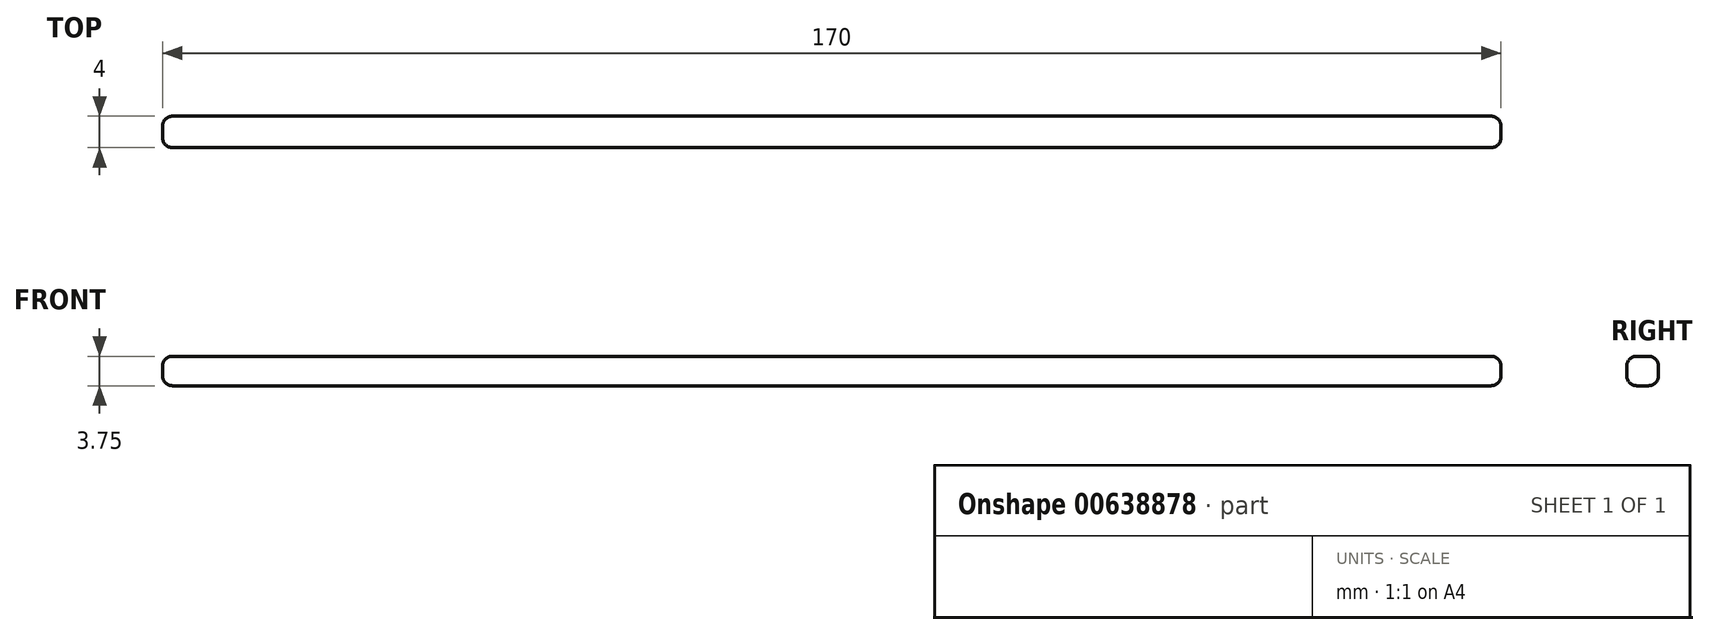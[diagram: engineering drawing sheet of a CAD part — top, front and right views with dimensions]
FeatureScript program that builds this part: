
annotation { "Feature Type Name" : "Feature", "Feature Type Description" : "" }
export const myFeature = defineFeature(function(context is Context, id is Id, definition is map)
    precondition{}
    {
        {
            var Q0;
            Q0=qCreatedBy(makeId("Top.planeOp"),FACE);
            var sketch = newSketch(context, id + "F0", { "sketchPlane" : qUnion([Q0])});
            skLineSegment(sketch, "E0.bottom", {"start": v(85, -2) * mm, "end": v(-85, -2) * mm});
            skLineSegment(sketch, "E0.top", {"start": v(85, 2) * mm, "end": v(-85, 2) * mm});
            skLineSegment(sketch, "E0.left", {"start": v(85, -2) * mm, "end": v(85, 2) * mm});
            skLineSegment(sketch, "E0.right", {"start": v(-85, -2) * mm, "end": v(-85, 2) * mm});
            skPoint(sketch, "E0.middle", {"position": v(0, 0) * mm});
            skSolve(sketch);
        }
        {
            var Q0;
            Q0=makeQuery(id+"F0.imprint","IMPRINT",FACE,{"disambiguationData":[TD([[makeQuery(id+"F0.imprint","IMPRINT",EDGE,{"derivedFrom":sQuery(id+"F0.wireOp",EDGE,"E0.bottom")}),-1.0]])]});
            extrude(context, id + "F1", {"entities" : qUnion([Q0]), "depth" : 3.75 * mm, "offsetDistance" : 25 * mm});
        }
        {
            var Q0;
            Q0=makeQuery(id+"F1.opExtrude","SWEPT_FACE",FACE,{"disambiguationData":[OSD([sQuery(id+"F0.wireOp",EDGE,"E0.right")])]});
            var Q1;
            Q1=makeQuery(id+"F1.opExtrude","SWEPT_FACE",FACE,{"disambiguationData":[OSD([sQuery(id+"F0.wireOp",EDGE,"E0.left")])]});
            var Q2;
            Q2=makeQuery(id+"F1.opExtrude","CAP_EDGE",EDGE,{"disambiguationData":[OSD([sQuery(id+"F0.wireOp",EDGE,"E0.bottom")])],"isStart":false});
            var Q3;
            Q3=makeQuery(id+"F1.opExtrude","CAP_EDGE",EDGE,{"disambiguationData":[OSD([sQuery(id+"F0.wireOp",EDGE,"E0.bottom")])],"isStart":true});
            var Q4;
            Q4=makeQuery(id+"F1.opExtrude","CAP_EDGE",EDGE,{"disambiguationData":[OSD([sQuery(id+"F0.wireOp",EDGE,"E0.top")])],"isStart":true});
            var Q5;
            Q5=makeQuery(id+"F1.opExtrude","CAP_EDGE",EDGE,{"disambiguationData":[OSD([sQuery(id+"F0.wireOp",EDGE,"E0.top")])],"isStart":false});
            fillet(context, id + "F2", {"entities" : qUnion([Q0, Q1, Q2, Q3, Q4, Q5]), "radius" : 1.25 * mm, "tangentPropagation" : true, "allowEdgeOverflow" : false});
        }
    });
